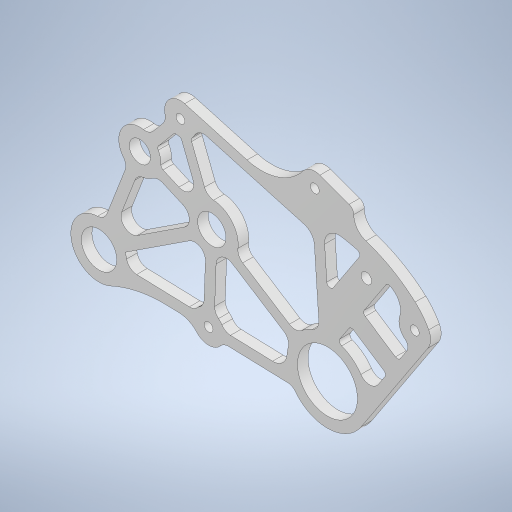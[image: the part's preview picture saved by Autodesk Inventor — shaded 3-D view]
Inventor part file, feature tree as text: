
AUTODESK INVENTOR PART (.ipt)
format: ipt  version: 2023.1 (Build 271208000, 208)  size: 607,744 bytes
history: native  units: mm
features: other x3, fillet x1, sketch x1
ambient origin geometry x8: Origin, YZ Plane, XZ Plane, XY Plane, X Axis, Y Axis, Z Axis, Center Point
bodies: Solid2 (feature_tree)
feature tree (5):
  other  "ギア抑え.ipt"
  fillet  "フィレット1"  Radius=10.0mm
  other  "Solid2::ギア抑え.ipt"
  other  "TaggingFeature1"
  sketch  "Sketch4"  dims[d1=1.0mm]
